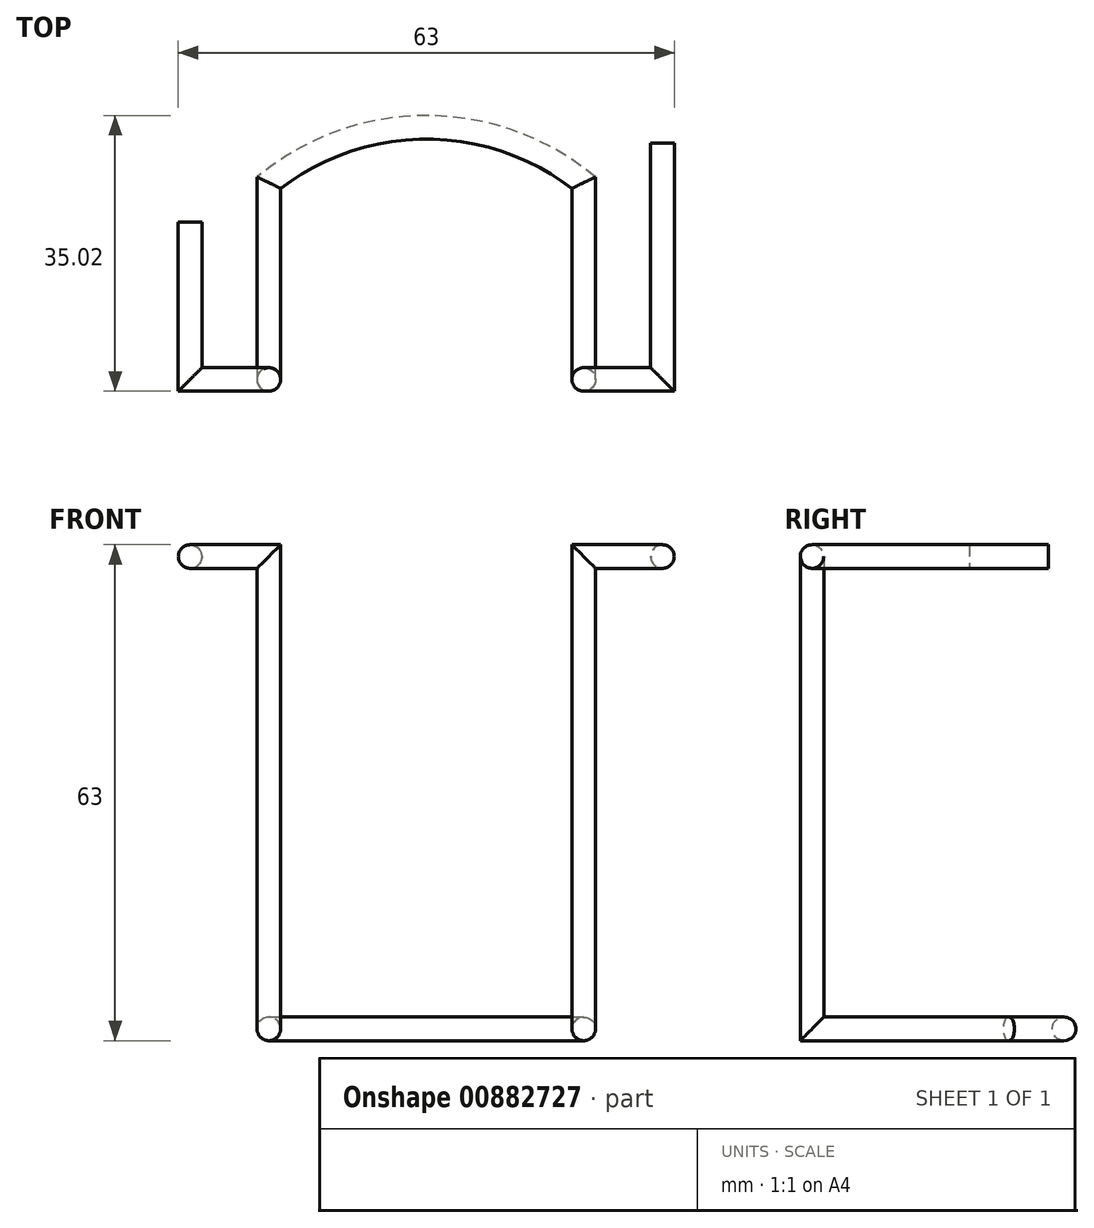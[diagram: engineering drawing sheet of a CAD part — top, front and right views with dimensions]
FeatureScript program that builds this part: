
annotation { "Feature Type Name" : "Feature", "Feature Type Description" : "" }
export const myFeature = defineFeature(function(context is Context, id is Id, definition is map)
    precondition{}
    {
        {
            var Q0;
            Q0=qCreatedBy(makeId("Front.planeOp"),FACE);
            cPlane(context, id + "F0", {"entities" : qUnion([Q0]), "cplaneType" : CPlaneType.OFFSET, "offset" : 30 * mm, "width" : 152.4 * mm, "height" : 152.4 * mm});
        }
        {
            var Q0;
            Q0=qCreatedBy(makeId("Top.planeOp"),FACE);
            cPlane(context, id + "F1", {"entities" : qUnion([Q0]), "cplaneType" : CPlaneType.OFFSET, "offset" : 60 * mm, "oppositeDirection" : true, "width" : 150 * mm, "height" : 150 * mm});
        }
        {
            var Q0;
            Q0=qCreatedBy(makeId("Top.planeOp"),FACE);
            var sketch = newSketch(context, id + "F2", { "sketchPlane" : qUnion([Q0])});
            skLineSegment(sketch, "E0", {"start": v(-30, -10) * mm, "end": v(-30, -30) * mm});
            skLineSegment(sketch, "E1", {"start": v(-30, -30) * mm, "end": v(-20, -30) * mm});
            skLineSegment(sketch, "E2", {"start": v(30, 0) * mm, "end": v(30, -30) * mm});
            skLineSegment(sketch, "E3", {"start": v(30, -30) * mm, "end": v(20, -30) * mm});
            skSolve(sketch);
        }
        {
            var Q0;
            Q0=qCreatedBy(id+"F0.planeOp",FACE);
            var sketch = newSketch(context, id + "F3", { "sketchPlane" : qUnion([Q0])});
            skPoint(sketch, "E4.0", {"position": v(-20, 0) * mm});
            skPoint(sketch, "E5.0", {"position": v(20, 0) * mm});
            skLineSegment(sketch, "E6", {"start": v(-20, 0) * mm, "end": v(-20, -60) * mm});
            skLineSegment(sketch, "E7", {"start": v(20, 0) * mm, "end": v(20, -60) * mm});
            skSolve(sketch);
        }
        {
            var Q0;
            Q0=qCreatedBy(id+"F1.planeOp",FACE);
            var sketch = newSketch(context, id + "F4", { "sketchPlane" : qUnion([Q0])});
            skPoint(sketch, "E8.0", {"position": v(-20, -30) * mm});
            skPoint(sketch, "E9.0", {"position": v(20, -30) * mm});
            skLineSegment(sketch, "E10", {"start": v(-20, -30) * mm, "end": v(-20, -5) * mm});
            skArc(sketch, "E11", {"start": v(20, -5) * mm, "mid": v(0, 2.02) * mm, "end": v(-20, -5) * mm});
            skLineSegment(sketch, "E12", {"start": v(20, -5) * mm, "end": v(20, -30) * mm});
            skSolve(sketch);
        }
        {
            var Q0;
            Q0=qCreatedBy(id+"F1.planeOp",FACE);
            var Q1;
            Q1=qCreatedBy(id+"F1.planeOp",FACE);
            var sketch = newSketch(context, id + "F5", { "sketchPlane" : qUnion([Q0, Q1])});
            skPoint(sketch, "E13.0", {"position": v(-20, -30) * mm});
            skCircle(sketch, "E14", {"center": v(-20, -30) * mm, "radius": 1.5 * mm});
            skSolve(sketch);
        }
        {
            var Q0;
            Q0 = qSketchRegion(id + "F5", true);
            var Q1;
            Q1 = qConstructionFilter(qBodyType(qCreatedBy(id + "F2" ,EDGE), BodyType.WIRE), ConstructionObject.NO);
            var Q2;
            Q2 = qConstructionFilter(qBodyType(qCreatedBy(id + "F3" ,EDGE), BodyType.WIRE), ConstructionObject.NO);
            var Q3;
            Q3 = qConstructionFilter(qBodyType(qCreatedBy(id + "F4" ,EDGE), BodyType.WIRE), ConstructionObject.NO);
            sweep(context, id + "F6", {"profiles" : qUnion([Q0]), "path" : qUnion([Q1, Q2, Q3])});
        }
    });
